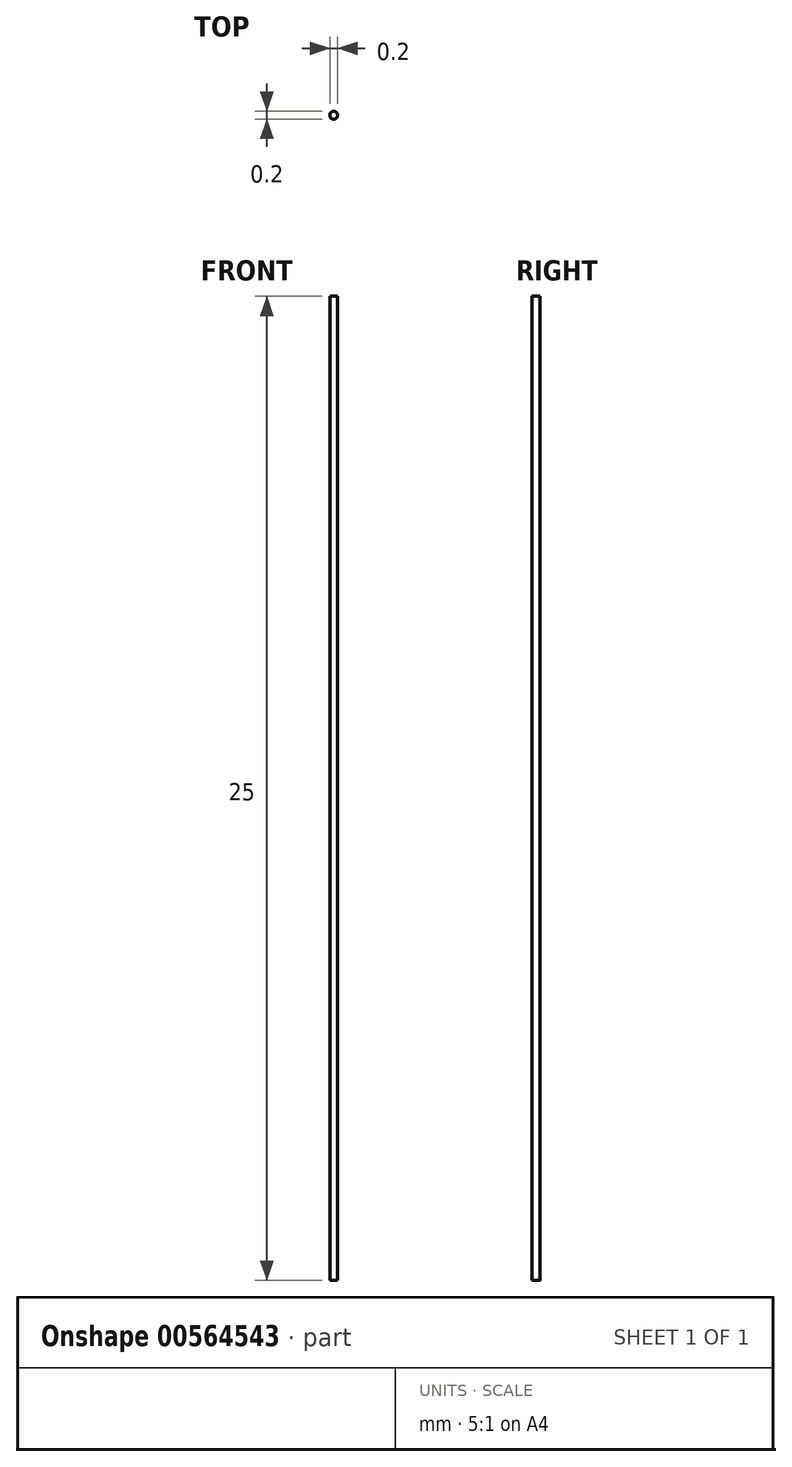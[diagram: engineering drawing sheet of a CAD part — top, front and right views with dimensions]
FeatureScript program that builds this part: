
annotation { "Feature Type Name" : "Feature", "Feature Type Description" : "" }
export const myFeature = defineFeature(function(context is Context, id is Id, definition is map)
    precondition{}
    {
        {
            var Q0;
            Q0=qCreatedBy(makeId("Top.planeOp"),FACE);
            var sketch = newSketch(context, id + "F0", { "sketchPlane" : qUnion([Q0])});
            skCircle(sketch, "E0", {"center": v(0, 0) * mm, "radius": 0.1 * mm});
            skSolve(sketch);
        }
        {
            var Q0;
            Q0 = qSketchRegion(id + "F0", true);
            extrude(context, id + "F1", {"entities" : qUnion([Q0]), "depth" : 25 * mm, "offsetDistance" : 25 * mm});
        }
    });
